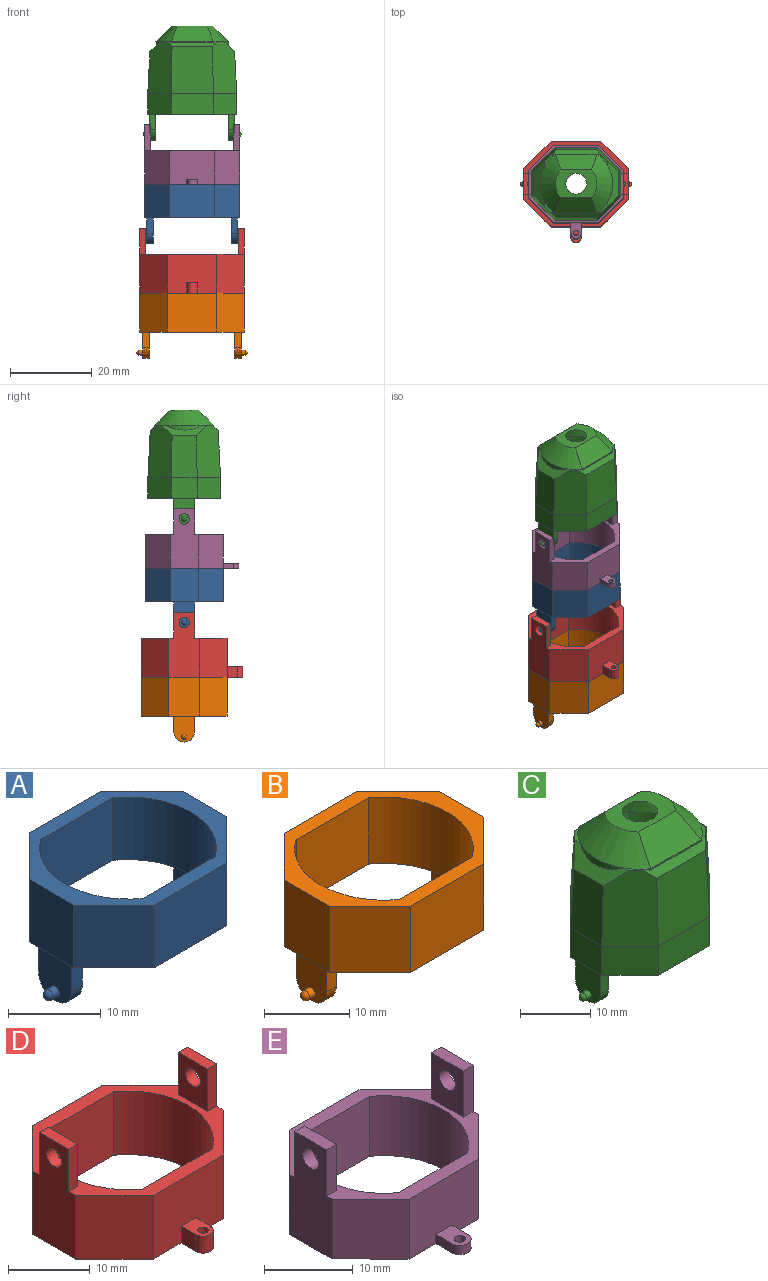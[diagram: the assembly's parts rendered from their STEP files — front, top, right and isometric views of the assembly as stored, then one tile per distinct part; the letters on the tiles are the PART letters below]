
ASSEMBLY  parts=5 mates=4
PART A: 28 faces, bbox 25.3x19.1x14.6 mm
  f0: plane 8.26x6.12mm, normal (-0.71,0.71,0), area 71.5mm2, adj f1,f11,f12,f27
  f1: plane 8.26x6.8mm, normal (-1,0,0), area 56.2mm2, adj f0,f2,f12,f27
  f2: plane 8.26x6.12mm, normal (-0.71,-0.71,0), area 71.5mm2, adj f1,f3,f12,f27
  f3: plane 11.08x8.26mm, normal (0,-1,0), area 91.5mm2, adj f2,f4,f12,f27
  f4: plane 8.26x6.12mm, normal (0.71,-0.71,0), area 71.5mm2, adj f3,f5,f12,f27
  f5: plane 8.26x6.8mm, normal (1,0,0), area 56.2mm2, adj f4,f6,f12,f27
  f6: plane 8.26x6.12mm, normal (0.71,0.71,0), area 71.5mm2, adj f5,f11,f12,f27
  f7: plane 10.95x8.26mm, normal (0,1,0), area 90.4mm2, adj f8,f10,f12,f27
  f8: cylinder r=9.53mm len=15.59mm, axis (0,0,-1), area 150.7mm2, adj f7,f9,f12,f27
  f9: plane 10.95x8.26mm, normal (0,-1,0), area 90.4mm2, adj f8,f10,f12,f27
  f10: cylinder r=9.53mm len=15.59mm, axis (0,0,-1), area 150.7mm2, adj f7,f9,f12,f27
  f11: plane 11.08x8.26mm, normal (0,1,0), area 91.5mm2, adj f0,f6,f12,f27
  f12: plane 23.33x19.05mm, normal (0,0,-1), area 94.3mm2, adj f0,f1,f2,f3,f4,f5,f6,f7
  f13: plane 6.35x5.08mm, normal (-1,0,0), area 29.5mm2, adj f12,f14,f16,f18
  f14: plane 3.81x1.57mm, normal (0,-1,0), area 6mm2, adj f12,f13,f15,f18
  f15: plane 6.35x5.08mm, normal (1,0,0), area 28.2mm2, adj f12,f14,f16,f17,f18
  f16: plane 3.81x1.57mm, normal (0,1,0), area 6mm2, adj f12,f13,f15,f18
  f17: cylinder r=0.64mm len=1.27mm, axis (-1,0,0), area 3.7mm2, adj f15,f19
  f18: cylinder r=2.54mm len=5.08mm, axis (1,0,0), area 12.5mm2, adj f13,f14,f15,f16
  f19: sphere r=0.64mm, area 2.5mm2, adj f17
  f20: sphere r=0.64mm, area 2.5mm2, adj f22
  f21: cylinder r=2.54mm len=5.08mm, axis (-1,0,0), area 12.5mm2, adj f23,f24,f25,f26
  f22: cylinder r=0.64mm len=1.27mm, axis (1,0,0), area 3.7mm2, adj f20,f24
  f23: plane 3.81x1.57mm, normal (0,1,0), area 6mm2, adj f12,f21,f24,f26
  f24: plane 6.35x5.08mm, normal (-1,0,0), area 28.2mm2, adj f12,f21,f22,f23,f25
  f25: plane 3.81x1.57mm, normal (0,-1,0), area 6mm2, adj f12,f21,f24,f26
  f26: plane 6.35x5.08mm, normal (1,0,0), area 29.5mm2, adj f12,f21,f23,f25
  f27: plane 23.33x19.05mm, normal (0,0,1), area 110.2mm2, adj f0,f1,f2,f3,f4,f5,f6,f7
PART B: 28 faces, bbox 27.2x21x15.9 mm
  f0: plane 9.53x6.74mm, normal (-0.71,0.71,0), area 90.7mm2, adj f1,f11,f12,f27
  f1: plane 9.53x7.48mm, normal (-1,0,0), area 71.3mm2, adj f0,f2,f12,f27
  f2: plane 9.53x6.74mm, normal (-0.71,-0.71,0), area 90.7mm2, adj f1,f3,f12,f27
  f3: plane 12.19x9.53mm, normal (0,-1,0), area 116.1mm2, adj f2,f4,f12,f27
  f4: plane 9.53x6.74mm, normal (0.71,-0.71,0), area 90.7mm2, adj f3,f5,f12,f27
  f5: plane 9.53x7.48mm, normal (1,0,0), area 71.3mm2, adj f4,f6,f12,f27
  f6: plane 9.53x6.74mm, normal (0.71,0.71,0), area 90.7mm2, adj f5,f11,f12,f27
  f7: plane 12.05x9.53mm, normal (0,1,0), area 114.8mm2, adj f8,f10,f12,f27
  f8: cylinder r=10.48mm len=17.15mm, axis (0,0,-1), area 191.3mm2, adj f7,f9,f12,f27
  f9: plane 12.05x9.53mm, normal (0,-1,0), area 114.8mm2, adj f8,f10,f12,f27
  f10: cylinder r=10.48mm len=17.15mm, axis (0,0,-1), area 191.3mm2, adj f7,f9,f12,f27
  f11: plane 12.19x9.53mm, normal (0,1,0), area 116.1mm2, adj f0,f6,f12,f27
  f12: plane 25.66x20.96mm, normal (0,0,-1), area 117.4mm2, adj f0,f1,f2,f3,f4,f5,f6,f7
  f13: plane 6.35x5.08mm, normal (-1,0,0), area 29.5mm2, adj f12,f14,f16,f18
  f14: plane 3.81x1.57mm, normal (0,-1,0), area 6mm2, adj f12,f13,f15,f18
  f15: plane 6.35x5.08mm, normal (1,0,0), area 28.2mm2, adj f12,f14,f16,f17,f18
  f16: plane 3.81x1.57mm, normal (0,1,0), area 6mm2, adj f12,f13,f15,f18
  f17: cylinder r=0.64mm len=1.27mm, axis (-1,0,0), area 3.7mm2, adj f15,f19
  f18: cylinder r=2.54mm len=5.08mm, axis (1,0,0), area 12.5mm2, adj f13,f14,f15,f16
  f19: sphere r=0.64mm, area 2.5mm2, adj f17
  f20: sphere r=0.64mm, area 2.5mm2, adj f22
  f21: cylinder r=2.54mm len=5.08mm, axis (-1,0,0), area 12.5mm2, adj f23,f24,f25,f26
  f22: cylinder r=0.64mm len=1.27mm, axis (1,0,0), area 3.7mm2, adj f20,f24
  f23: plane 3.81x1.57mm, normal (0,1,0), area 6mm2, adj f12,f21,f24,f26
  f24: plane 6.35x5.08mm, normal (-1,0,0), area 28.2mm2, adj f12,f21,f22,f23,f25
  f25: plane 3.81x1.57mm, normal (0,-1,0), area 6mm2, adj f12,f21,f24,f26
  f26: plane 6.35x5.08mm, normal (1,0,0), area 29.5mm2, adj f12,f21,f23,f25
  f27: plane 25.66x20.96mm, normal (0,0,1), area 133.4mm2, adj f0,f1,f2,f3,f4,f5,f6,f7
PART C: 57 faces, bbox 24.1x17.8x27.9 mm
  f0: plane 16.86x10.22mm, normal (0,1,0), area 166.6mm2, adj f2,f13,f14,f56
  f1: plane 16.86x10.22mm, normal (0,-1,0), area 166.6mm2, adj f2,f13,f14,f56
  f2: plane 21.77x17.78mm, normal (0,0,-1), area 80.1mm2, adj f0,f1,f6,f7,f8,f9,f10,f11
  f3: plane 2.56x2.21mm, normal (0,0,1), area 1.3mm2, adj f28,f33,f35,f52
  f4: plane 2.56x2.21mm, normal (0,0,1), area 1.3mm2, adj f27,f32,f34,f55
  f5: plane 2.56x2.21mm, normal (0,0,1), area 1.3mm2, adj f24,f32,f35,f55
  f6: plane 5.71x5.71mm, normal (-0.71,0.71,0), area 41.1mm2, adj f2,f7,f15,f31
  f7: plane 6.35x5.08mm, normal (-1,0,0), area 32.3mm2, adj f2,f6,f8,f30
  f8: plane 5.71x5.71mm, normal (-0.71,-0.71,0), area 41.1mm2, adj f2,f7,f9,f28
  f9: plane 10.34x5.08mm, normal (0,-1,0), area 52.6mm2, adj f2,f8,f10,f26
  f10: plane 5.71x5.71mm, normal (0.71,-0.71,0), area 41.1mm2, adj f2,f9,f11,f24
  f11: plane 6.35x5.08mm, normal (1,0,0), area 32.3mm2, adj f2,f10,f12,f25
  f12: plane 5.71x5.71mm, normal (0.71,0.71,0), area 41.1mm2, adj f2,f11,f15,f27
  f13: cylinder r=8.89mm len=15.24mm, axis (0,0,-1), area 259.7mm2, adj f0,f1,f2,f56
  f14: cylinder r=8.89mm len=15.24mm, axis (0,0,-1), area 259.7mm2, adj f0,f1,f2,f56
  f15: plane 10.34x5.08mm, normal (0,1,0), area 52.6mm2, adj f2,f6,f12,f29
  f16: plane 2.56x2.21mm, normal (0,0,1), area 1.3mm2, adj f31,f33,f34,f52
  f17: plane 6.35x5.08mm, normal (-1,0,0), area 29.5mm2, adj f2,f18,f20,f22
  f18: plane 3.81x1.57mm, normal (0,-1,0), area 6mm2, adj f2,f17,f19,f22
  f19: plane 6.35x5.08mm, normal (1,0,0), area 28.2mm2, adj f2,f18,f20,f21,f22
  f20: plane 3.81x1.57mm, normal (0,1,0), area 6mm2, adj f2,f17,f19,f22
  f21: cylinder r=0.64mm len=1.27mm, axis (-1,0,0), area 3.7mm2, adj f19,f23
  f22: cylinder r=2.54mm len=5.08mm, axis (1,0,0), area 12.5mm2, adj f17,f18,f19,f20
  f23: sphere r=0.64mm, area 2.5mm2, adj f21
  f24: plane 12.7x5.95mm, normal (0.71,-0.71,0.05), area 93.7mm2, adj f5,f10,f25,f26,f32,f35
  f25: plane 10.16x6.35mm, normal (1,0,0.05), area 62.5mm2, adj f11,f24,f27,f32
  f26: plane 11.43x10.34mm, normal (0,-1,0.05), area 115.7mm2, adj f9,f24,f28,f35
  f27: plane 12.7x5.95mm, normal (0.71,0.71,0.05), area 93.7mm2, adj f4,f12,f25,f29,f32,f34
  f28: plane 12.7x5.95mm, normal (-0.71,-0.71,0.05), area 93.7mm2, adj f3,f8,f26,f30,f33,f35
  f29: plane 11.43x10.34mm, normal (0,1,0.05), area 115.7mm2, adj f15,f27,f31,f34
  f30: plane 10.16x6.35mm, normal (-1,0,0.05), area 62.5mm2, adj f7,f28,f31,f33
  f31: plane 12.7x5.95mm, normal (-0.71,0.71,0.05), area 93.7mm2, adj f6,f16,f29,f30,f33,f34
  f32: plane 10.9x2.67mm, normal (0.69,0,0.72), area 21.3mm2, adj f4,f5,f24,f25,f27,f44
  f33: plane 10.9x2.67mm, normal (-0.69,0,0.72), area 21.3mm2, adj f3,f16,f28,f30,f31,f45
  f34: plane 12.36x1.34mm, normal (0,0.69,0.72), area 16.2mm2, adj f4,f16,f27,f29,f31,f48,f49,f50
  f35: plane 12.36x1.34mm, normal (0,-0.69,0.72), area 16.2mm2, adj f3,f5,f24,f26,f28,f43,f46,f47
  f36: sphere r=0.64mm, area 2.5mm2, adj f38
  f37: cylinder r=2.54mm len=5.08mm, axis (-1,0,0), area 12.5mm2, adj f39,f40,f41,f42
  f38: cylinder r=0.64mm len=1.27mm, axis (1,0,0), area 3.7mm2, adj f36,f40
  f39: plane 3.81x1.57mm, normal (0,1,0), area 6mm2, adj f2,f37,f40,f42
  f40: plane 6.35x5.08mm, normal (-1,0,0), area 28.2mm2, adj f2,f37,f38,f39,f41
  f41: plane 3.81x1.57mm, normal (0,-1,0), area 6mm2, adj f2,f37,f40,f42
  f42: plane 6.35x5.08mm, normal (1,0,0), area 29.5mm2, adj f2,f37,f39,f41
  f43: cylinder r=8.89mm len=0.39mm, axis (0,0,-1), area 0.1mm2, adj f35,f47,f55
  f44: cylinder r=8.89mm len=8.84mm, axis (0,0,-1), area 6.9mm2, adj f32,f55
  f45: cylinder r=8.89mm len=8.84mm, axis (0,0,-1), area 6.9mm2, adj f33,f52
  f46: cylinder r=8.89mm len=0.39mm, axis (0,0,-1), area 0.1mm2, adj f35,f47,f52
  f47: plane 10.22x0.27mm, normal (0,-1,0), area 2.8mm2, adj f35,f43,f46,f54
  f48: cylinder r=8.89mm len=0.39mm, axis (0,0,-1), area 0.1mm2, adj f34,f49,f55
  f49: plane 10.22x0.27mm, normal (0,1,0), area 2.8mm2, adj f34,f48,f50,f53
  f50: cylinder r=8.89mm len=0.39mm, axis (0,0,-1), area 0.1mm2, adj f34,f49,f52
  f51: plane 10.16x6.93mm, normal (0,0,1), area 44.2mm2, adj f52,f53,f54,f55,f56
  f52: cone r=8.89mm half-angle=45deg, axis (0,0,-1), area 66.1mm2, adj f3,f16,f45,f46,f50,f51,f53,f54
  f53: plane 10.22x3.81mm, normal (0,0.71,0.71), area 48mm2, adj f49,f51,f52,f55
  f54: plane 10.22x3.81mm, normal (0,-0.71,0.71), area 48mm2, adj f47,f51,f52,f55
  f55: cone r=8.89mm half-angle=45deg, axis (0,0,-1), area 66.1mm2, adj f4,f5,f43,f44,f48,f51,f53,f54
  f56: cone r=2.54mm half-angle=45deg, axis (0,0,-1), area 290.7mm2, adj f0,f1,f13,f14,f51
PART D: 29 faces, bbox 25.7x24.8x15.9 mm
  f0: plane 9.53x6.74mm, normal (-0.71,0.71,0), area 90.7mm2, adj f1,f11,f12,f23
  f1: plane 15.88x7.48mm, normal (-1,0,0), area 98.5mm2, adj f0,f2,f12,f19,f20,f21,f22,f23
  f2: plane 9.53x6.74mm, normal (-0.71,-0.71,0), area 90.7mm2, adj f1,f3,f12,f23
  f3: plane 12.19x9.53mm, normal (0,-1,0), area 109.7mm2, adj f2,f4,f12,f23,f24,f26,f28
  f4: plane 9.53x6.74mm, normal (0.71,-0.71,0), area 90.7mm2, adj f3,f5,f12,f23
  f5: plane 15.88x7.48mm, normal (1,0,0), area 98.5mm2, adj f4,f6,f12,f14,f15,f16,f17,f23
  f6: plane 9.53x6.74mm, normal (0.71,0.71,0), area 90.7mm2, adj f5,f11,f12,f23
  f7: plane 12.05x9.53mm, normal (0,1,0), area 114.8mm2, adj f8,f10,f12,f23
  f8: cylinder r=10.48mm len=17.15mm, axis (0,0,-1), area 191.3mm2, adj f7,f9,f12,f23
  f9: plane 12.05x9.53mm, normal (0,-1,0), area 114.8mm2, adj f8,f10,f12,f23
  f10: cylinder r=10.48mm len=17.15mm, axis (0,0,-1), area 191.3mm2, adj f7,f9,f12,f23
  f11: plane 12.19x9.53mm, normal (0,1,0), area 116.1mm2, adj f0,f6,f12,f23
  f12: plane 25.66x20.96mm, normal (0,0,1), area 117.4mm2, adj f0,f1,f2,f3,f4,f5,f6,f7
  f13: plane 6.35x5.08mm, normal (-1,0,0), area 27.2mm2, adj f12,f14,f15,f16,f17
  f14: plane 6.35x1.57mm, normal (0,-1,0), area 10mm2, adj f5,f12,f13,f16
  f15: plane 6.35x1.57mm, normal (0,1,0), area 10mm2, adj f5,f12,f13,f16
  f16: plane 5.08x1.57mm, normal (0,0,1), area 8mm2, adj f5,f13,f14,f15
  f17: cylinder r=1.27mm len=2.54mm, axis (1,0,0), area 12.5mm2, adj f5,f13
  f18: plane 6.35x5.08mm, normal (1,0,0), area 27.2mm2, adj f12,f19,f20,f21,f22
  f19: plane 6.35x1.57mm, normal (0,-1,0), area 10mm2, adj f1,f12,f18,f21
  f20: plane 6.35x1.57mm, normal (0,1,0), area 10mm2, adj f1,f12,f18,f21
  f21: plane 5.08x1.57mm, normal (0,0,1), area 8mm2, adj f1,f18,f19,f20
  f22: cylinder r=1.27mm len=2.54mm, axis (-1,0,0), area 12.5mm2, adj f1,f18
  f23: plane 25.66x24.77mm, normal (0,0,-1), area 141.1mm2, adj f0,f1,f2,f3,f4,f5,f6,f7
  f24: plane 2.54x2.54mm, normal (1,0,0), area 6.5mm2, adj f3,f23,f25,f28
  f25: cylinder r=1.27mm len=2.54mm, axis (0,0,-1), area 10.1mm2, adj f23,f24,f26,f28
  f26: plane 2.54x2.54mm, normal (-1,0,0), area 6.5mm2, adj f3,f23,f25,f28
  f27: cylinder r=0.64mm len=2.54mm, axis (0,0,-1), area 10.1mm2, adj f23,f28
  f28: plane 3.81x2.54mm, normal (0,0,1), area 7.7mm2, adj f3,f24,f25,f26,f27
PART E: 29 faces, bbox 23.3x22.9x14.6 mm
  f0: plane 8.26x6.12mm, normal (-0.71,0.71,0), area 71.5mm2, adj f1,f9,f11,f23
  f1: plane 14.61x6.8mm, normal (-1,0,0), area 83.4mm2, adj f0,f2,f11,f19,f20,f21,f22,f23
  f2: plane 8.26x6.12mm, normal (-0.71,-0.71,0), area 71.5mm2, adj f1,f3,f11,f23
  f3: plane 11.08x8.26mm, normal (0,-1,0), area 88.3mm2, adj f2,f4,f11,f23,f24,f26,f28
  f4: plane 8.26x6.12mm, normal (0.71,-0.71,0), area 71.5mm2, adj f3,f5,f11,f23
  f5: plane 14.61x6.8mm, normal (1,0,0), area 83.4mm2, adj f4,f6,f11,f14,f15,f16,f17,f23
  f6: plane 8.26x6.12mm, normal (0.71,0.71,0), area 71.5mm2, adj f5,f9,f11,f23
  f7: cylinder r=9.53mm len=15.59mm, axis (0,0,-1), area 150.7mm2, adj f10,f11,f12,f23
  f8: cylinder r=9.53mm len=15.59mm, axis (0,0,-1), area 150.7mm2, adj f10,f11,f12,f23
  f9: plane 11.08x8.26mm, normal (0,1,0), area 91.5mm2, adj f0,f6,f11,f23
  f10: plane 10.95x8.26mm, normal (0,-1,0), area 90.4mm2, adj f7,f8,f11,f23
  f11: plane 23.33x19.05mm, normal (0,0,1), area 94.3mm2, adj f0,f1,f2,f3,f4,f5,f6,f7
  f12: plane 10.95x8.26mm, normal (0,1,0), area 90.4mm2, adj f7,f8,f11,f23
  f13: plane 6.35x5.08mm, normal (-1,0,0), area 27.2mm2, adj f11,f14,f15,f16,f17
  f14: plane 6.35x1.57mm, normal (0,-1,0), area 10mm2, adj f5,f11,f13,f16
  f15: plane 6.35x1.57mm, normal (0,1,0), area 10mm2, adj f5,f11,f13,f16
  f16: plane 5.08x1.57mm, normal (0,0,1), area 8mm2, adj f5,f13,f14,f15
  f17: cylinder r=1.27mm len=2.54mm, axis (1,0,0), area 12.5mm2, adj f5,f13
  f18: plane 6.35x5.08mm, normal (1,0,0), area 27.2mm2, adj f11,f19,f20,f21,f22
  f19: plane 6.35x1.57mm, normal (0,-1,0), area 10mm2, adj f1,f11,f18,f21
  f20: plane 6.35x1.57mm, normal (0,1,0), area 10mm2, adj f1,f11,f18,f21
  f21: plane 5.08x1.57mm, normal (0,0,1), area 8mm2, adj f1,f18,f19,f20
  f22: cylinder r=1.27mm len=2.54mm, axis (-1,0,0), area 12.5mm2, adj f1,f18
  f23: plane 23.33x22.86mm, normal (0,0,-1), area 117.9mm2, adj f0,f1,f2,f3,f4,f5,f6,f7
  f24: plane 2.54x1.27mm, normal (1,0,0), area 3.2mm2, adj f3,f23,f25,f28
  f25: cylinder r=1.27mm len=2.54mm, axis (0,0,-1), area 5.1mm2, adj f23,f24,f26,f28
  f26: plane 2.54x1.27mm, normal (-1,0,0), area 3.2mm2, adj f3,f23,f25,f28
  f27: cylinder r=0.64mm len=1.27mm, axis (0,0,-1), area 5.1mm2, adj f23,f28
  f28: plane 3.81x2.54mm, normal (0,0,1), area 7.7mm2, adj f3,f24,f25,f26,f27
PLACE A t=(34.65,-4.14,-9.82)mm
PLACE B t=(34.61,-4.14,-37.76)mm
PLACE C t=(34.66,-4.14,15.58)mm
PLACE D t=(34.61,-4.14,-37.76)mm
PLACE E t=(34.65,-4.14,-9.82)mm
MATE fastened D.f4 <-> B.f4  axis (0.71,-0.71,0) through (44.07,-11.25,-28.24)mm
MATE revolute C.f21 <-> E.f17  axis (1,0,0) through (45.12,-4.14,10.5)mm
MATE fastened E.f4 <-> A.f4  axis (0.71,-0.71,0) through (43.25,-10.6,-1.57)mm
MATE revolute A.f17 <-> D.f17  axis (1,0,0) through (45.74,-4.14,-14.9)mm
